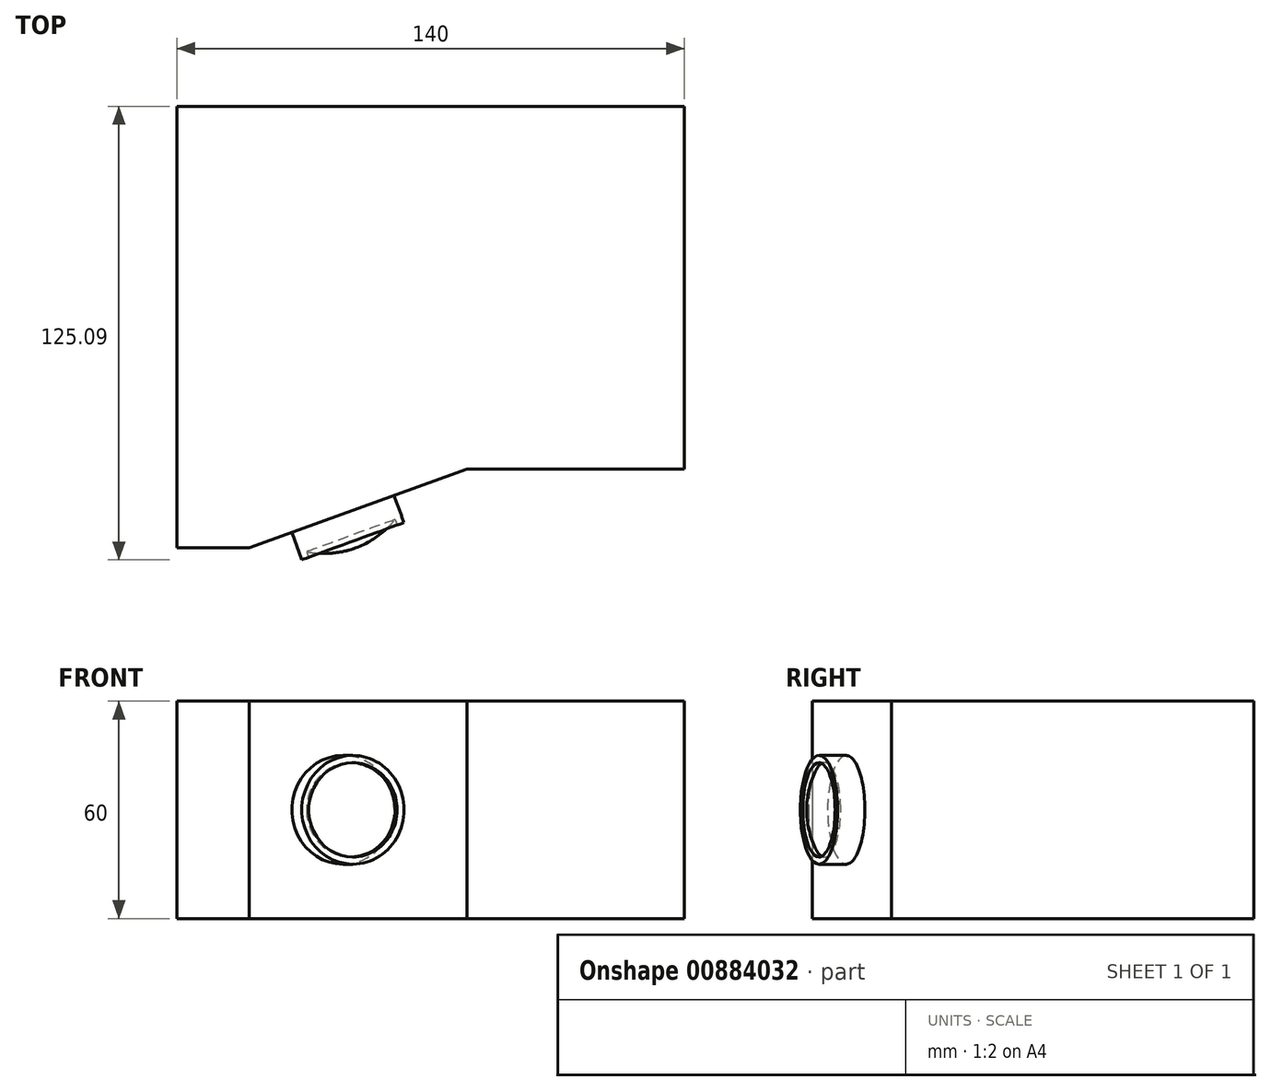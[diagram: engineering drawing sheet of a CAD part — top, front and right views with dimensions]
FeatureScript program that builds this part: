
annotation { "Feature Type Name" : "Feature", "Feature Type Description" : "" }
export const myFeature = defineFeature(function(context is Context, id is Id, definition is map)
    precondition{}
    {
        {
            var Q0;
            Q0=qCreatedBy(makeId("Top.planeOp"),FACE);
            var sketch = newSketch(context, id + "F0", { "sketchPlane" : qUnion([Q0])});
            skLineSegment(sketch, "E0", {"start": v(-140, 0) * mm, "end": v(-140, 121.84) * mm});
            skLineSegment(sketch, "E1", {"start": v(-140, 121.84) * mm, "end": v(0, 121.84) * mm});
            skLineSegment(sketch, "E2", {"start": v(0, 121.84) * mm, "end": v(0, 21.84) * mm});
            skLineSegment(sketch, "E3", {"start": v(0, 21.84) * mm, "end": v(-60, 21.84) * mm});
            skLineSegment(sketch, "E4", {"start": v(-60, 21.84) * mm, "end": v(-120, 0) * mm});
            skLineSegment(sketch, "E5", {"start": v(-120, 0) * mm, "end": v(-140, 0) * mm});
            skSolve(sketch);
        }
        {
            var Q0;
            Q0=makeQuery(id+"F0.imprint","IMPRINT",FACE,{"disambiguationData":[TD([[makeQuery(id+"F0.imprint","IMPRINT",EDGE,{"derivedFrom":sQuery(id+"F0.wireOp",EDGE,"E0")}),-1.0]])]});
            extrude(context, id + "F1", {"entities" : qUnion([Q0]), "endBound" : BoundingType.SYMMETRIC, "depth" : 60 * mm, "offsetDistance" : 25 * mm});
        }
        {
            var Q0;
            Q0=qCreatedBy(makeId("Top.planeOp"),FACE);
            var sketch = newSketch(context, id + "F2", { "sketchPlane" : qUnion([Q0])});
            skLineSegment(sketch, "E6", {"start": v(-108.28, 4.27) * mm, "end": v(-94.18, 9.4) * mm});
            skArc(sketch, "E7", {"start": v(-104.22, -1.02) * mm, "mid": v(-97.42, -1.44) * mm, "end": v(-90.76, 0) * mm});
            skLineSegment(sketch, "E8", {"start": v(-104.22, -1.02) * mm, "end": v(-103.66, -2.57) * mm});
            skLineSegment(sketch, "E9", {"start": v(-103.66, -2.57) * mm, "end": v(-105.54, -3.25) * mm});
            skLineSegment(sketch, "E10", {"start": v(-105.54, -3.25) * mm, "end": v(-108.28, 4.27) * mm});
            skLineSegment(sketch, "E11", {"start": v(-104.22, -1.02) * mm, "end": v(-92, 3.43) * mm, "construction": true});
            skLineSegment(sketch, "E12", {"start": v(-90.76, 0) * mm, "end": v(-94.18, 9.4) * mm});
            skLineSegment(sketch, "E13", {"start": v(-90.76, 0) * mm, "end": v(-102.98, -4.45) * mm, "construction": true});
            skLineSegment(sketch, "E14", {"start": v(-102.98, -4.45) * mm, "end": v(-103.66, -2.57) * mm, "construction": true});
            skSolve(sketch);
        }
        {
            var Q0;
            Q0 = qSketchRegion(id + "F2", true);
            var Q1;
            Q1=sQuery(id+"F2.wireOp",EDGE,"E12");
            revolve(context, id + "F3", {"surfaceOperationType" : NewSurfaceOperationType.NEW, "entities" : qUnion([Q0]), "axis" : qUnion([Q1]), "revolveType" : RevolveType.FULL});
        }
    });
